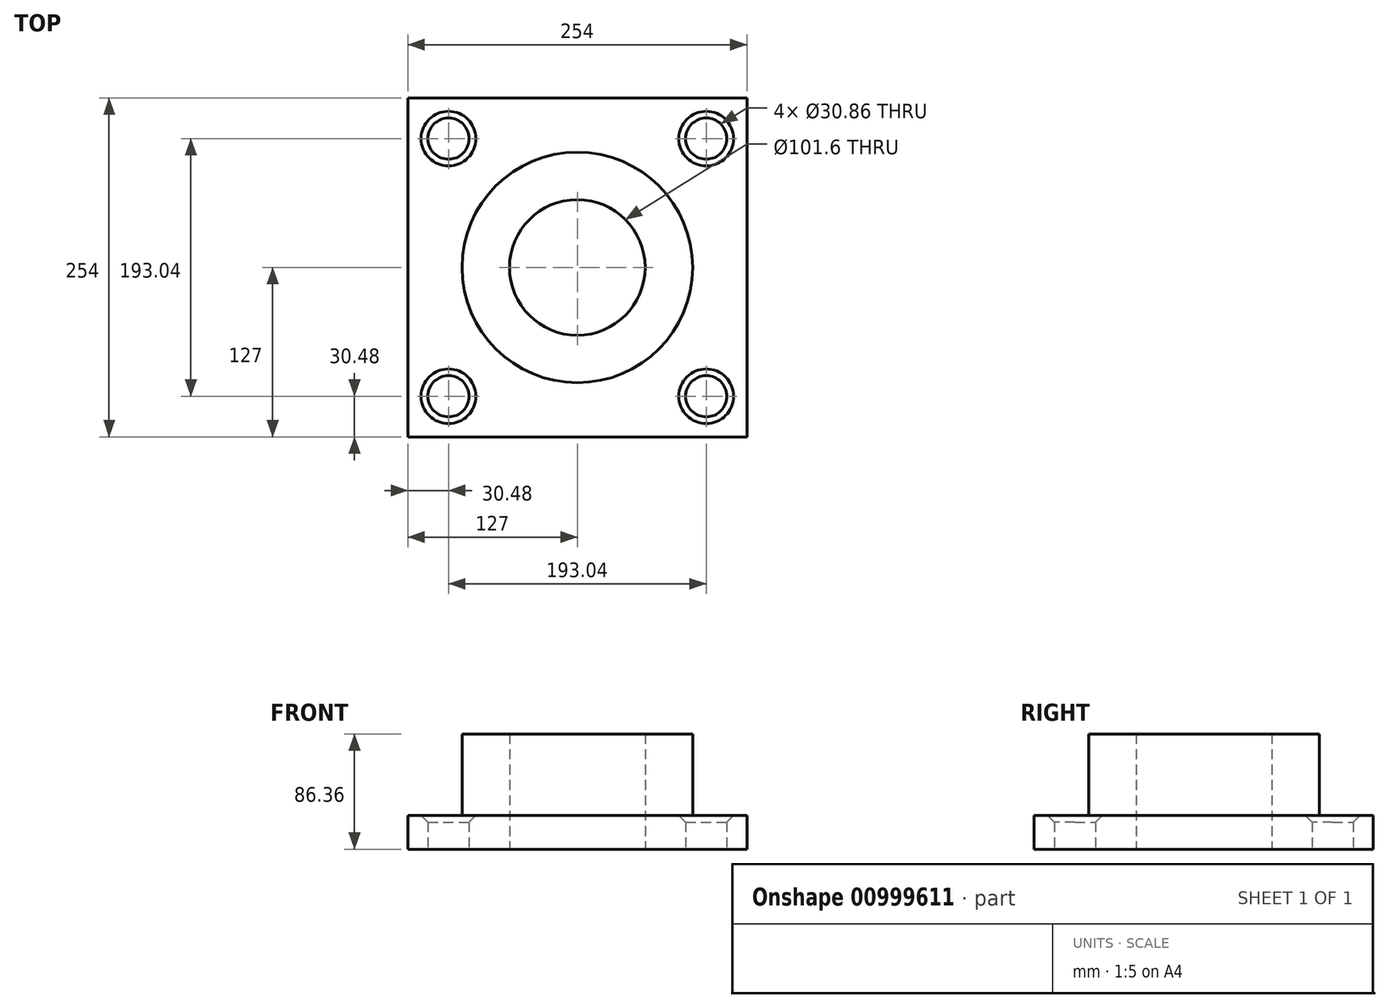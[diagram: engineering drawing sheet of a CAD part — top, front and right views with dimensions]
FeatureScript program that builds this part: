
annotation { "Feature Type Name" : "Feature", "Feature Type Description" : "" }
export const myFeature = defineFeature(function(context is Context, id is Id, definition is map)
    precondition{}
    {
        {
            var Q0;
            Q0=qCreatedBy(makeId("Top.planeOp"),FACE);
            var sketch = newSketch(context, id + "F0", { "sketchPlane" : qUnion([Q0])});
            skLineSegment(sketch, "E0.bottom", {"start": v(127, -127) * mm, "end": v(-127, -127) * mm});
            skLineSegment(sketch, "E0.top", {"start": v(127, 127) * mm, "end": v(-127, 127) * mm});
            skLineSegment(sketch, "E0.left", {"start": v(127, -127) * mm, "end": v(127, 127) * mm});
            skLineSegment(sketch, "E0.right", {"start": v(-127, -127) * mm, "end": v(-127, 127) * mm});
            skPoint(sketch, "E0.middle", {"position": v(0, 0) * mm});
            skCircle(sketch, "E1", {"center": v(0, 0) * mm, "radius": 50.8 * mm});
            skSolve(sketch);
        }
        {
            var Q0;
            Q0=makeQuery(id+"F0.imprint","IMPRINT",FACE,{"disambiguationData":[TD([[makeQuery(id+"F0.imprint","IMPRINT",EDGE,{"derivedFrom":sQuery(id+"F0.wireOp",EDGE,"E0.bottom")}),-1.0]])]});
            extrude(context, id + "F1", {"entities" : qUnion([Q0]), "depth" : 25.4 * mm, "offsetDistance" : 25.4 * mm});
        }
        {
            var Q0;
            Q0=makeQuery(id+"F1.opExtrude","CAP_FACE",FACE,{"disambiguationData":[OSD([sQuery(id+"F0.wireOp",EDGE,"E0.bottom"),sQuery(id+"F0.wireOp",EDGE,"E0.top"),sQuery(id+"F0.wireOp",EDGE,"E0.left"),sQuery(id+"F0.wireOp",EDGE,"E0.right"),sQuery(id+"F0.wireOp",EDGE,"E1")])],"isStart":false});
            var sketch = newSketch(context, id + "F2", { "sketchPlane" : qUnion([Q0])});
            skCircle(sketch, "E2.0", {"center": v(0, 0) * mm, "radius": 50.8 * mm});
            skCircle(sketch, "E3.0", {"center": v(0, 0) * mm, "radius": 86.36 * mm});
            skSolve(sketch);
        }
        {
            var Q0;
            Q0=makeQuery(id+"F2.imprint","IMPRINT",FACE,{"disambiguationData":[TD([[makeQuery(id+"F2.imprint","IMPRINT",EDGE,{"derivedFrom":sQuery(id+"F2.wireOp",EDGE,"E2.0")}),-1.0]])]});
            extrude(context, id + "F3", {"entities" : qUnion([Q0]), "operationType" : NewBodyOperationType.ADD, "depth" : 60.96 * mm, "offsetDistance" : 25.4 * mm});
        }
        {
            var Q0;
            Q0=makeQuery(id+"F1.opExtrude","CAP_FACE",FACE,{"disambiguationData":[OSD([sQuery(id+"F0.wireOp",EDGE,"E0.bottom"),sQuery(id+"F0.wireOp",EDGE,"E0.top"),sQuery(id+"F0.wireOp",EDGE,"E0.left"),sQuery(id+"F0.wireOp",EDGE,"E0.right"),sQuery(id+"F0.wireOp",EDGE,"E1")])],"isStart":true});
            var sketch = newSketch(context, id + "F4", { "sketchPlane" : qUnion([Q0])});
            skLineSegment(sketch, "E4.0", {"start": v(96.52, -96.52) * mm, "end": v(-96.52, -96.52) * mm, "construction": true});
            skLineSegment(sketch, "E4.1", {"start": v(96.52, 96.52) * mm, "end": v(96.52, -96.52) * mm, "construction": true});
            skLineSegment(sketch, "E4.2", {"start": v(96.52, 96.52) * mm, "end": v(-96.52, 96.52) * mm, "construction": true});
            skLineSegment(sketch, "E4.3", {"start": v(-96.52, 96.52) * mm, "end": v(-96.52, -96.52) * mm, "construction": true});
            skCircle(sketch, "E5", {"center": v(-96.52, -96.52) * mm, "radius": 15.43 * mm});
            skCircle(sketch, "E6", {"center": v(-96.52, 96.52) * mm, "radius": 15.43 * mm});
            skCircle(sketch, "E7", {"center": v(96.52, 96.52) * mm, "radius": 15.43 * mm});
            skCircle(sketch, "E8", {"center": v(96.52, -96.52) * mm, "radius": 15.43 * mm});
            skSolve(sketch);
        }
        {
            var Q0;
            Q0=makeQuery(id+"F4.imprint","IMPRINT",FACE,{"disambiguationData":[TD([[makeQuery(id+"F4.imprint","IMPRINT",EDGE,{"derivedFrom":sQuery(id+"F4.wireOp",EDGE,"E5")}),1.0]])]});
            var Q1;
            Q1=makeQuery(id+"F4.imprint","IMPRINT",FACE,{"disambiguationData":[TD([[makeQuery(id+"F4.imprint","IMPRINT",EDGE,{"derivedFrom":sQuery(id+"F4.wireOp",EDGE,"E8")}),1.0]])]});
            var Q2;
            Q2=makeQuery(id+"F4.imprint","IMPRINT",FACE,{"disambiguationData":[TD([[makeQuery(id+"F4.imprint","IMPRINT",EDGE,{"derivedFrom":sQuery(id+"F4.wireOp",EDGE,"E7")}),1.0]])]});
            var Q3;
            Q3=makeQuery(id+"F4.imprint","IMPRINT",FACE,{"disambiguationData":[TD([[makeQuery(id+"F4.imprint","IMPRINT",EDGE,{"derivedFrom":sQuery(id+"F4.wireOp",EDGE,"E6")}),1.0]])]});
            var Q4;
            Q4 = qConstructionFilter(qBodyType(qCreatedBy(id + "F4" ,EDGE), BodyType.WIRE), ConstructionObject.NO);
            extrude(context, id + "F5", {"entities" : qUnion([Q0, Q1, Q2, Q3]), "operationType" : NewBodyOperationType.REMOVE, "surfaceEntities" : qUnion([Q4]), "oppositeDirection" : true, "depth" : 162.56 * mm, "offsetDistance" : 25.4 * mm});
        }
        {
            var Q0;
            Q0=makeQuery(id+"F5.boolean.opBoolean","INTERSECT",EDGE,{"derivedFrom":[makeQuery(id+"F1.opExtrude","CAP_FACE",FACE,{"disambiguationData":[OSD([sQuery(id+"F0.wireOp",EDGE,"E0.bottom"),sQuery(id+"F0.wireOp",EDGE,"E0.top"),sQuery(id+"F0.wireOp",EDGE,"E0.left"),sQuery(id+"F0.wireOp",EDGE,"E0.right"),sQuery(id+"F0.wireOp",EDGE,"E1")])],"isStart":false}),makeQuery(id+"F5.opExtrude","SWEPT_FACE",FACE,{"disambiguationData":[OSD([sQuery(id+"F4.wireOp",EDGE,"E5")])]})]});
            var Q1;
            Q1=makeQuery(id+"F5.boolean.opBoolean","INTERSECT",EDGE,{"derivedFrom":[makeQuery(id+"F1.opExtrude","CAP_FACE",FACE,{"disambiguationData":[OSD([sQuery(id+"F0.wireOp",EDGE,"E0.bottom"),sQuery(id+"F0.wireOp",EDGE,"E0.top"),sQuery(id+"F0.wireOp",EDGE,"E0.left"),sQuery(id+"F0.wireOp",EDGE,"E0.right"),sQuery(id+"F0.wireOp",EDGE,"E1")])],"isStart":false}),makeQuery(id+"F5.opExtrude","SWEPT_FACE",FACE,{"disambiguationData":[OSD([sQuery(id+"F4.wireOp",EDGE,"E8")])]})]});
            var Q2;
            Q2=makeQuery(id+"F5.boolean.opBoolean","INTERSECT",EDGE,{"derivedFrom":[makeQuery(id+"F1.opExtrude","CAP_FACE",FACE,{"disambiguationData":[OSD([sQuery(id+"F0.wireOp",EDGE,"E0.bottom"),sQuery(id+"F0.wireOp",EDGE,"E0.top"),sQuery(id+"F0.wireOp",EDGE,"E0.left"),sQuery(id+"F0.wireOp",EDGE,"E0.right"),sQuery(id+"F0.wireOp",EDGE,"E1")])],"isStart":false}),makeQuery(id+"F5.opExtrude","SWEPT_FACE",FACE,{"disambiguationData":[OSD([sQuery(id+"F4.wireOp",EDGE,"E7")])]})]});
            var Q3;
            Q3=makeQuery(id+"F5.boolean.opBoolean","INTERSECT",EDGE,{"derivedFrom":[makeQuery(id+"F1.opExtrude","CAP_FACE",FACE,{"disambiguationData":[OSD([sQuery(id+"F0.wireOp",EDGE,"E0.bottom"),sQuery(id+"F0.wireOp",EDGE,"E0.top"),sQuery(id+"F0.wireOp",EDGE,"E0.left"),sQuery(id+"F0.wireOp",EDGE,"E0.right"),sQuery(id+"F0.wireOp",EDGE,"E1")])],"isStart":false}),makeQuery(id+"F5.opExtrude","SWEPT_FACE",FACE,{"disambiguationData":[OSD([sQuery(id+"F4.wireOp",EDGE,"E6")])]})]});
            chamfer(context, id + "F6", {"entities" : qUnion([Q0, Q1, Q2, Q3]), "width" : 5.08 * mm, "tangentPropagation" : true});
        }
    });
